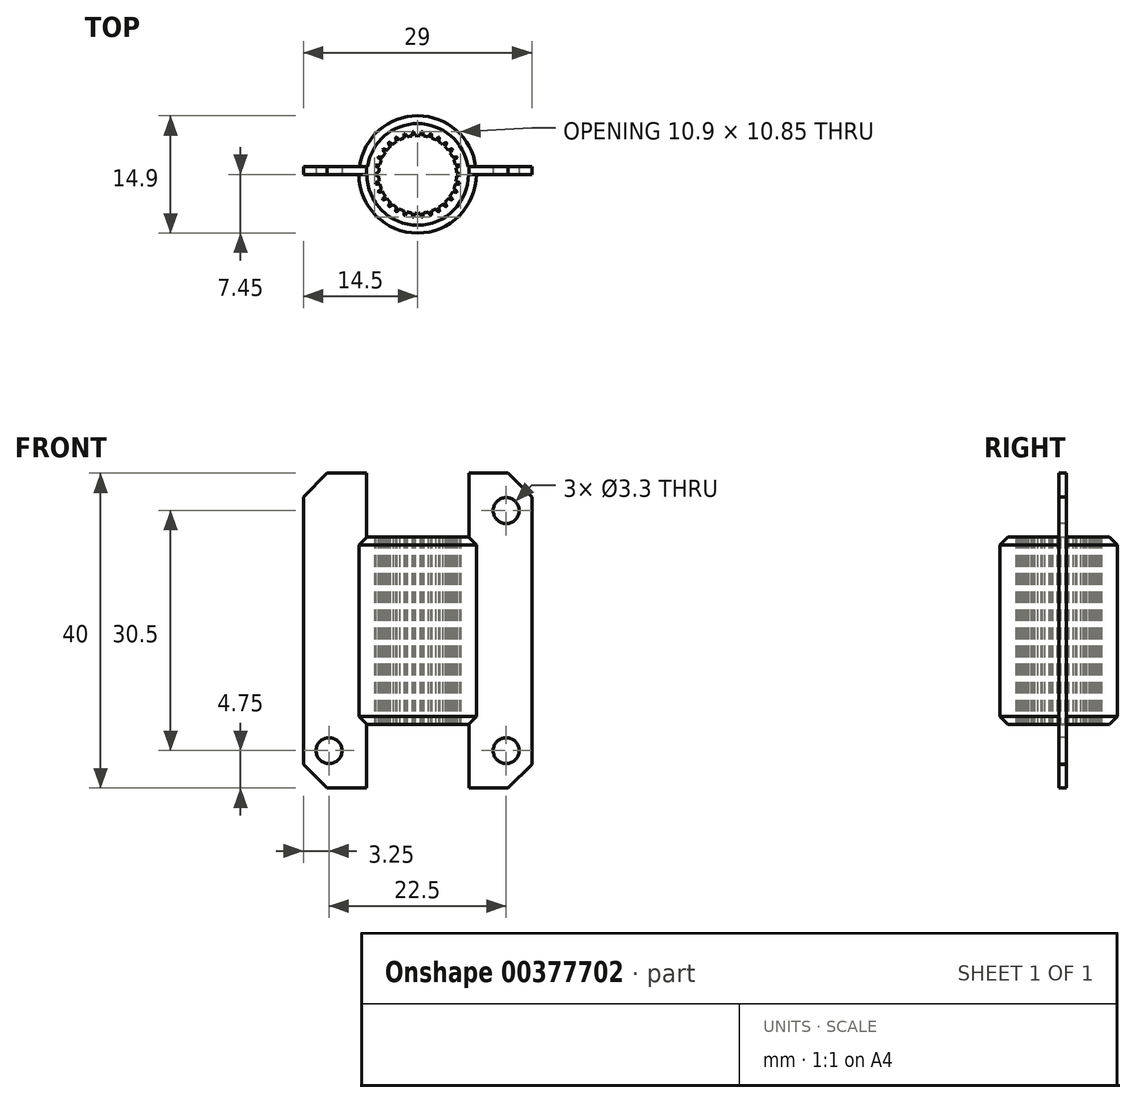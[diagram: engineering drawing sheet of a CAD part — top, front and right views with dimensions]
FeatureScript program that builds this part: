
annotation { "Feature Type Name" : "Feature", "Feature Type Description" : "" }
export const myFeature = defineFeature(function(context is Context, id is Id, definition is map)
    precondition{}
    {
        {
            var Q0;
            Q0=qCreatedBy(makeId("Top.planeOp"),FACE);
            var sketch = newSketch(context, id + "F0", { "sketchPlane" : qUnion([Q0])});
            skCircle(sketch, "E0", {"center": v(0, 0) * mm, "radius": 4.95 * mm, "construction": true});
            skCircle(sketch, "E1", {"center": v(0, 0) * mm, "radius": 7.45 * mm});
            skCircle(sketch, "E2.0", {"center": v(0, 0) * mm, "radius": 5.45 * mm});
            skLineSegment(sketch, "E3", {"start": v(0, 0) * mm, "end": v(0, 9.5) * mm, "construction": true});
            skLineSegment(sketch, "E4", {"start": v(0.5, 5.43) * mm, "end": v(0.3, 4.94) * mm});
            skArc(sketch, "E5", {"start": v(0.3, 4.94) * mm, "mid": v(0.15, 4.95) * mm, "end": v(0, 4.95) * mm});
            skLineSegment(sketch, "E6.MirrorCS", {"start": v(-0.5, 5.43) * mm, "end": v(-0.3, 4.94) * mm});
            skArc(sketch, "E7.MirrorCS", {"start": v(-0.3, 4.94) * mm, "mid": v(-0.15, 4.95) * mm, "end": v(0, 4.95) * mm});
            skLineSegment(sketch, "E8.1.0", {"start": v(-0.64, 5.41) * mm, "end": v(-0.73, 4.9) * mm});
            skLineSegment(sketch, "E8.1.1", {"start": v(-1.62, 5.2) * mm, "end": v(-1.32, 4.77) * mm});
            skArc(sketch, "E8.1.2", {"start": v(-0.73, 4.9) * mm, "mid": v(-0.88, 4.87) * mm, "end": v(-1.03, 4.84) * mm});
            skArc(sketch, "E8.1.3", {"start": v(-1.32, 4.77) * mm, "mid": v(-1.18, 4.8) * mm, "end": v(-1.03, 4.84) * mm});
            skLineSegment(sketch, "E8.2.0", {"start": v(-1.75, 5.16) * mm, "end": v(-1.74, 4.64) * mm});
            skLineSegment(sketch, "E8.2.1", {"start": v(-2.66, 4.75) * mm, "end": v(-2.28, 4.4) * mm});
            skArc(sketch, "E8.2.2", {"start": v(-1.74, 4.64) * mm, "mid": v(-1.88, 4.58) * mm, "end": v(-2.01, 4.52) * mm});
            skArc(sketch, "E8.2.3", {"start": v(-2.28, 4.4) * mm, "mid": v(-2.15, 4.46) * mm, "end": v(-2.01, 4.52) * mm});
            skLineSegment(sketch, "E8.3.0", {"start": v(-2.79, 4.68) * mm, "end": v(-2.66, 4.17) * mm});
            skLineSegment(sketch, "E8.3.1", {"start": v(-3.6, 4.1) * mm, "end": v(-3.15, 3.82) * mm});
            skArc(sketch, "E8.3.2", {"start": v(-2.66, 4.17) * mm, "mid": v(-2.79, 4.1) * mm, "end": v(-2.9, 4) * mm});
            skArc(sketch, "E8.3.3", {"start": v(-3.15, 3.82) * mm, "mid": v(-3.03, 3.91) * mm, "end": v(-2.9, 4) * mm});
            skLineSegment(sketch, "E8.4.0", {"start": v(-3.7, 4) * mm, "end": v(-3.47, 3.53) * mm});
            skLineSegment(sketch, "E8.4.1", {"start": v(-4.37, 3.26) * mm, "end": v(-3.87, 3.08) * mm});
            skArc(sketch, "E8.4.2", {"start": v(-3.47, 3.53) * mm, "mid": v(-3.58, 3.42) * mm, "end": v(-3.68, 3.31) * mm});
            skArc(sketch, "E8.4.3", {"start": v(-3.87, 3.08) * mm, "mid": v(-3.78, 3.2) * mm, "end": v(-3.68, 3.31) * mm});
            skLineSegment(sketch, "E8.5.0", {"start": v(-4.45, 3.15) * mm, "end": v(-4.13, 2.73) * mm});
            skLineSegment(sketch, "E8.5.1", {"start": v(-4.95, 2.28) * mm, "end": v(-4.43, 2.21) * mm});
            skArc(sketch, "E8.5.2", {"start": v(-4.13, 2.73) * mm, "mid": v(-4.2, 2.6) * mm, "end": v(-4.29, 2.48) * mm});
            skArc(sketch, "E8.5.3", {"start": v(-4.43, 2.21) * mm, "mid": v(-4.36, 2.34) * mm, "end": v(-4.29, 2.48) * mm});
            skLineSegment(sketch, "E8.6.0", {"start": v(-5, 2.15) * mm, "end": v(-4.6, 1.81) * mm});
            skLineSegment(sketch, "E8.6.1", {"start": v(-5.32, 1.2) * mm, "end": v(-4.8, 1.24) * mm});
            skArc(sketch, "E8.6.2", {"start": v(-4.6, 1.81) * mm, "mid": v(-4.66, 1.67) * mm, "end": v(-4.7, 1.53) * mm});
            skArc(sketch, "E8.6.3", {"start": v(-4.8, 1.24) * mm, "mid": v(-4.75, 1.39) * mm, "end": v(-4.7, 1.53) * mm});
            skLineSegment(sketch, "E8.7.0", {"start": v(-5.35, 1.06) * mm, "end": v(-4.88, 0.81) * mm});
            skLineSegment(sketch, "E8.7.1", {"start": v(-5.45, 0.07) * mm, "end": v(-4.95, 0.22) * mm});
            skArc(sketch, "E8.7.2", {"start": v(-4.88, 0.81) * mm, "mid": v(-4.9, 0.67) * mm, "end": v(-4.92, 0.52) * mm});
            skArc(sketch, "E8.7.3", {"start": v(-4.95, 0.22) * mm, "mid": v(-4.94, 0.37) * mm, "end": v(-4.92, 0.52) * mm});
            skLineSegment(sketch, "E8.8.0", {"start": v(-5.45, -0.07) * mm, "end": v(-4.95, -0.22) * mm});
            skLineSegment(sketch, "E8.8.1", {"start": v(-5.35, -1.06) * mm, "end": v(-4.88, -0.81) * mm});
            skArc(sketch, "E8.8.2", {"start": v(-4.95, -0.22) * mm, "mid": v(-4.94, -0.37) * mm, "end": v(-4.92, -0.52) * mm});
            skArc(sketch, "E8.8.3", {"start": v(-4.88, -0.81) * mm, "mid": v(-4.9, -0.67) * mm, "end": v(-4.92, -0.52) * mm});
            skLineSegment(sketch, "E8.9.0", {"start": v(-5.32, -1.2) * mm, "end": v(-4.8, -1.24) * mm});
            skLineSegment(sketch, "E8.9.1", {"start": v(-5, -2.15) * mm, "end": v(-4.6, -1.81) * mm});
            skArc(sketch, "E8.9.2", {"start": v(-4.8, -1.24) * mm, "mid": v(-4.75, -1.39) * mm, "end": v(-4.7, -1.53) * mm});
            skArc(sketch, "E8.9.3", {"start": v(-4.6, -1.81) * mm, "mid": v(-4.66, -1.67) * mm, "end": v(-4.7, -1.53) * mm});
            skLineSegment(sketch, "E8.10.0", {"start": v(-4.95, -2.28) * mm, "end": v(-4.43, -2.21) * mm});
            skLineSegment(sketch, "E8.10.1", {"start": v(-4.45, -3.15) * mm, "end": v(-4.13, -2.73) * mm});
            skArc(sketch, "E8.10.2", {"start": v(-4.43, -2.21) * mm, "mid": v(-4.36, -2.34) * mm, "end": v(-4.29, -2.47) * mm});
            skArc(sketch, "E8.10.3", {"start": v(-4.13, -2.73) * mm, "mid": v(-4.2, -2.6) * mm, "end": v(-4.29, -2.47) * mm});
            skLineSegment(sketch, "E8.11.0", {"start": v(-4.37, -3.26) * mm, "end": v(-3.87, -3.08) * mm});
            skLineSegment(sketch, "E8.11.1", {"start": v(-3.7, -4) * mm, "end": v(-3.47, -3.53) * mm});
            skArc(sketch, "E8.11.2", {"start": v(-3.87, -3.08) * mm, "mid": v(-3.78, -3.2) * mm, "end": v(-3.68, -3.31) * mm});
            skArc(sketch, "E8.11.3", {"start": v(-3.47, -3.53) * mm, "mid": v(-3.58, -3.42) * mm, "end": v(-3.68, -3.31) * mm});
            skLineSegment(sketch, "E8.12.0", {"start": v(-3.6, -4.1) * mm, "end": v(-3.15, -3.82) * mm});
            skLineSegment(sketch, "E8.12.1", {"start": v(-2.79, -4.68) * mm, "end": v(-2.66, -4.17) * mm});
            skArc(sketch, "E8.12.2", {"start": v(-3.15, -3.82) * mm, "mid": v(-3.03, -3.91) * mm, "end": v(-2.9, -4) * mm});
            skArc(sketch, "E8.12.3", {"start": v(-2.66, -4.17) * mm, "mid": v(-2.79, -4.1) * mm, "end": v(-2.9, -4) * mm});
            skLineSegment(sketch, "E8.13.0", {"start": v(-2.66, -4.75) * mm, "end": v(-2.28, -4.4) * mm});
            skLineSegment(sketch, "E8.13.1", {"start": v(-1.75, -5.16) * mm, "end": v(-1.74, -4.64) * mm});
            skArc(sketch, "E8.13.2", {"start": v(-2.28, -4.4) * mm, "mid": v(-2.15, -4.46) * mm, "end": v(-2.01, -4.52) * mm});
            skArc(sketch, "E8.13.3", {"start": v(-1.74, -4.64) * mm, "mid": v(-1.88, -4.58) * mm, "end": v(-2.01, -4.52) * mm});
            skLineSegment(sketch, "E8.14.0", {"start": v(-1.62, -5.2) * mm, "end": v(-1.32, -4.77) * mm});
            skLineSegment(sketch, "E8.14.1", {"start": v(-0.64, -5.41) * mm, "end": v(-0.73, -4.9) * mm});
            skArc(sketch, "E8.14.2", {"start": v(-1.32, -4.77) * mm, "mid": v(-1.18, -4.8) * mm, "end": v(-1.03, -4.84) * mm});
            skArc(sketch, "E8.14.3", {"start": v(-0.73, -4.9) * mm, "mid": v(-0.88, -4.87) * mm, "end": v(-1.03, -4.84) * mm});
            skLineSegment(sketch, "E8.15.0", {"start": v(-0.5, -5.43) * mm, "end": v(-0.3, -4.94) * mm});
            skLineSegment(sketch, "E8.15.1", {"start": v(0.5, -5.43) * mm, "end": v(0.3, -4.94) * mm});
            skArc(sketch, "E8.15.2", {"start": v(-0.3, -4.94) * mm, "mid": v(-0.15, -4.95) * mm, "end": v(0, -4.95) * mm});
            skArc(sketch, "E8.15.3", {"start": v(0.3, -4.94) * mm, "mid": v(0.15, -4.95) * mm, "end": v(0, -4.95) * mm});
            skLineSegment(sketch, "E8.16.0", {"start": v(0.64, -5.41) * mm, "end": v(0.73, -4.9) * mm});
            skLineSegment(sketch, "E8.16.1", {"start": v(1.62, -5.2) * mm, "end": v(1.32, -4.77) * mm});
            skArc(sketch, "E8.16.2", {"start": v(0.73, -4.9) * mm, "mid": v(0.88, -4.87) * mm, "end": v(1.03, -4.84) * mm});
            skArc(sketch, "E8.16.3", {"start": v(1.32, -4.77) * mm, "mid": v(1.18, -4.8) * mm, "end": v(1.03, -4.84) * mm});
            skLineSegment(sketch, "E8.17.0", {"start": v(1.75, -5.16) * mm, "end": v(1.74, -4.64) * mm});
            skLineSegment(sketch, "E8.17.1", {"start": v(2.66, -4.75) * mm, "end": v(2.28, -4.4) * mm});
            skArc(sketch, "E8.17.2", {"start": v(1.74, -4.64) * mm, "mid": v(1.88, -4.58) * mm, "end": v(2.01, -4.52) * mm});
            skArc(sketch, "E8.17.3", {"start": v(2.28, -4.4) * mm, "mid": v(2.15, -4.46) * mm, "end": v(2.01, -4.52) * mm});
            skLineSegment(sketch, "E8.18.0", {"start": v(2.79, -4.68) * mm, "end": v(2.66, -4.17) * mm});
            skLineSegment(sketch, "E8.18.1", {"start": v(3.6, -4.1) * mm, "end": v(3.15, -3.82) * mm});
            skArc(sketch, "E8.18.2", {"start": v(2.66, -4.17) * mm, "mid": v(2.79, -4.1) * mm, "end": v(2.9, -4) * mm});
            skArc(sketch, "E8.18.3", {"start": v(3.15, -3.82) * mm, "mid": v(3.03, -3.91) * mm, "end": v(2.9, -4) * mm});
            skLineSegment(sketch, "E8.19.0", {"start": v(3.7, -4) * mm, "end": v(3.47, -3.53) * mm});
            skLineSegment(sketch, "E8.19.1", {"start": v(4.37, -3.26) * mm, "end": v(3.87, -3.08) * mm});
            skArc(sketch, "E8.19.2", {"start": v(3.47, -3.53) * mm, "mid": v(3.58, -3.42) * mm, "end": v(3.68, -3.31) * mm});
            skArc(sketch, "E8.19.3", {"start": v(3.87, -3.08) * mm, "mid": v(3.78, -3.2) * mm, "end": v(3.68, -3.31) * mm});
            skLineSegment(sketch, "E8.20.0", {"start": v(4.45, -3.15) * mm, "end": v(4.13, -2.73) * mm});
            skLineSegment(sketch, "E8.20.1", {"start": v(4.95, -2.28) * mm, "end": v(4.43, -2.21) * mm});
            skArc(sketch, "E8.20.2", {"start": v(4.13, -2.73) * mm, "mid": v(4.2, -2.6) * mm, "end": v(4.29, -2.48) * mm});
            skArc(sketch, "E8.20.3", {"start": v(4.43, -2.21) * mm, "mid": v(4.36, -2.34) * mm, "end": v(4.29, -2.48) * mm});
            skLineSegment(sketch, "E8.21.0", {"start": v(5, -2.15) * mm, "end": v(4.6, -1.81) * mm});
            skLineSegment(sketch, "E8.21.1", {"start": v(5.32, -1.2) * mm, "end": v(4.8, -1.24) * mm});
            skArc(sketch, "E8.21.2", {"start": v(4.6, -1.81) * mm, "mid": v(4.66, -1.67) * mm, "end": v(4.7, -1.53) * mm});
            skArc(sketch, "E8.21.3", {"start": v(4.8, -1.24) * mm, "mid": v(4.75, -1.39) * mm, "end": v(4.7, -1.53) * mm});
            skLineSegment(sketch, "E8.22.0", {"start": v(5.35, -1.06) * mm, "end": v(4.88, -0.81) * mm});
            skLineSegment(sketch, "E8.22.1", {"start": v(5.45, -0.07) * mm, "end": v(4.95, -0.22) * mm});
            skArc(sketch, "E8.22.2", {"start": v(4.88, -0.81) * mm, "mid": v(4.9, -0.67) * mm, "end": v(4.92, -0.52) * mm});
            skArc(sketch, "E8.22.3", {"start": v(4.95, -0.22) * mm, "mid": v(4.94, -0.37) * mm, "end": v(4.92, -0.52) * mm});
            skLineSegment(sketch, "E8.23.0", {"start": v(5.45, 0.07) * mm, "end": v(4.95, 0.22) * mm});
            skLineSegment(sketch, "E8.23.1", {"start": v(5.35, 1.06) * mm, "end": v(4.88, 0.81) * mm});
            skArc(sketch, "E8.23.2", {"start": v(4.95, 0.22) * mm, "mid": v(4.94, 0.37) * mm, "end": v(4.92, 0.52) * mm});
            skArc(sketch, "E8.23.3", {"start": v(4.88, 0.81) * mm, "mid": v(4.9, 0.67) * mm, "end": v(4.92, 0.52) * mm});
            skLineSegment(sketch, "E8.24.0", {"start": v(5.32, 1.2) * mm, "end": v(4.8, 1.24) * mm});
            skLineSegment(sketch, "E8.24.1", {"start": v(5, 2.15) * mm, "end": v(4.6, 1.81) * mm});
            skArc(sketch, "E8.24.2", {"start": v(4.8, 1.24) * mm, "mid": v(4.75, 1.39) * mm, "end": v(4.7, 1.53) * mm});
            skArc(sketch, "E8.24.3", {"start": v(4.6, 1.81) * mm, "mid": v(4.66, 1.67) * mm, "end": v(4.7, 1.53) * mm});
            skLineSegment(sketch, "E8.25.0", {"start": v(4.95, 2.28) * mm, "end": v(4.43, 2.21) * mm});
            skLineSegment(sketch, "E8.25.1", {"start": v(4.45, 3.15) * mm, "end": v(4.13, 2.73) * mm});
            skArc(sketch, "E8.25.2", {"start": v(4.43, 2.21) * mm, "mid": v(4.36, 2.34) * mm, "end": v(4.29, 2.47) * mm});
            skArc(sketch, "E8.25.3", {"start": v(4.13, 2.73) * mm, "mid": v(4.2, 2.6) * mm, "end": v(4.29, 2.47) * mm});
            skLineSegment(sketch, "E8.26.0", {"start": v(4.37, 3.26) * mm, "end": v(3.87, 3.08) * mm});
            skLineSegment(sketch, "E8.26.1", {"start": v(3.7, 4) * mm, "end": v(3.47, 3.53) * mm});
            skArc(sketch, "E8.26.2", {"start": v(3.87, 3.08) * mm, "mid": v(3.78, 3.2) * mm, "end": v(3.68, 3.31) * mm});
            skArc(sketch, "E8.26.3", {"start": v(3.47, 3.53) * mm, "mid": v(3.58, 3.42) * mm, "end": v(3.68, 3.31) * mm});
            skLineSegment(sketch, "E8.27.0", {"start": v(3.6, 4.1) * mm, "end": v(3.15, 3.82) * mm});
            skLineSegment(sketch, "E8.27.1", {"start": v(2.79, 4.68) * mm, "end": v(2.66, 4.17) * mm});
            skArc(sketch, "E8.27.2", {"start": v(3.15, 3.82) * mm, "mid": v(3.03, 3.91) * mm, "end": v(2.9, 4) * mm});
            skArc(sketch, "E8.27.3", {"start": v(2.66, 4.17) * mm, "mid": v(2.79, 4.1) * mm, "end": v(2.9, 4) * mm});
            skLineSegment(sketch, "E8.28.0", {"start": v(2.66, 4.75) * mm, "end": v(2.28, 4.4) * mm});
            skLineSegment(sketch, "E8.28.1", {"start": v(1.75, 5.16) * mm, "end": v(1.74, 4.64) * mm});
            skArc(sketch, "E8.28.2", {"start": v(2.28, 4.4) * mm, "mid": v(2.15, 4.46) * mm, "end": v(2.01, 4.52) * mm});
            skArc(sketch, "E8.28.3", {"start": v(1.74, 4.64) * mm, "mid": v(1.88, 4.58) * mm, "end": v(2.01, 4.52) * mm});
            skLineSegment(sketch, "E8.29.0", {"start": v(1.62, 5.2) * mm, "end": v(1.32, 4.77) * mm});
            skLineSegment(sketch, "E8.29.1", {"start": v(0.64, 5.41) * mm, "end": v(0.73, 4.9) * mm});
            skArc(sketch, "E8.29.2", {"start": v(1.32, 4.77) * mm, "mid": v(1.18, 4.8) * mm, "end": v(1.03, 4.84) * mm});
            skArc(sketch, "E8.29.3", {"start": v(0.73, 4.9) * mm, "mid": v(0.88, 4.87) * mm, "end": v(1.03, 4.84) * mm});
            skSolve(sketch);
        }
        {
            var Q0;
            {var subQ0=sQuery(id+"F0.wireOp",EDGE,"E8.4.0");Q0=makeQuery(id+"F0.imprint","IMPRINT",FACE,{"disambiguationData":[TD([[makeQuery(id+"F0.imprint","IMPRINT",EDGE,{"derivedFrom":subQ0}),-1.0]])]});}
            var Q1;
            {var subQ1=sQuery(id+"F0.wireOp",EDGE,"E8.5.0");Q1=makeQuery(id+"F0.imprint","IMPRINT",FACE,{"disambiguationData":[TD([[makeQuery(id+"F0.imprint","IMPRINT",EDGE,{"derivedFrom":subQ1}),-1.0]])]});}
            var Q2;
            {var subQ1=sQuery(id+"F0.wireOp",EDGE,"E8.3.0");Q2=makeQuery(id+"F0.imprint","IMPRINT",FACE,{"disambiguationData":[TD([[makeQuery(id+"F0.imprint","IMPRINT",EDGE,{"derivedFrom":subQ1}),-1.0]])]});}
            var Q3;
            {var subQ1=sQuery(id+"F0.wireOp",EDGE,"E8.2.0");Q3=makeQuery(id+"F0.imprint","IMPRINT",FACE,{"disambiguationData":[TD([[makeQuery(id+"F0.imprint","IMPRINT",EDGE,{"derivedFrom":subQ1}),-1.0]])]});}
            var Q4;
            {var subQ1=sQuery(id+"F0.wireOp",EDGE,"E8.1.0");Q4=makeQuery(id+"F0.imprint","IMPRINT",FACE,{"disambiguationData":[TD([[makeQuery(id+"F0.imprint","IMPRINT",EDGE,{"derivedFrom":subQ1}),-1.0]])]});}
            var Q5;
            {var subQ1=sQuery(id+"F0.wireOp",EDGE,"E4");Q5=makeQuery(id+"F0.imprint","IMPRINT",FACE,{"disambiguationData":[TD([[makeQuery(id+"F0.imprint","IMPRINT",EDGE,{"derivedFrom":subQ1}),-1.0]])]});}
            var Q6;
            {var subQ0=sQuery(id+"F0.wireOp",EDGE,"E8.29.0");Q6=makeQuery(id+"F0.imprint","IMPRINT",FACE,{"disambiguationData":[TD([[makeQuery(id+"F0.imprint","IMPRINT",EDGE,{"derivedFrom":subQ0}),-1.0]])]});}
            var Q7;
            Q7=makeQuery(id+"F0.imprint","IMPRINT",FACE,{"disambiguationData":[TD([[makeQuery(id+"F0.imprint","IMPRINT",EDGE,{"derivedFrom":sQuery(id+"F0.wireOp",EDGE,"E1")}),1.0]])]});
            var Q8;
            {var subQ1=sQuery(id+"F0.wireOp",EDGE,"E8.28.0");Q8=makeQuery(id+"F0.imprint","IMPRINT",FACE,{"disambiguationData":[TD([[makeQuery(id+"F0.imprint","IMPRINT",EDGE,{"derivedFrom":subQ1}),-1.0]])]});}
            var Q9;
            {var subQ1=sQuery(id+"F0.wireOp",EDGE,"E8.27.0");Q9=makeQuery(id+"F0.imprint","IMPRINT",FACE,{"disambiguationData":[TD([[makeQuery(id+"F0.imprint","IMPRINT",EDGE,{"derivedFrom":subQ1}),-1.0]])]});}
            var Q10;
            {var subQ1=sQuery(id+"F0.wireOp",EDGE,"E8.26.0");Q10=makeQuery(id+"F0.imprint","IMPRINT",FACE,{"disambiguationData":[TD([[makeQuery(id+"F0.imprint","IMPRINT",EDGE,{"derivedFrom":subQ1}),-1.0]])]});}
            var Q11;
            {var subQ1=sQuery(id+"F0.wireOp",EDGE,"E8.25.0");Q11=makeQuery(id+"F0.imprint","IMPRINT",FACE,{"disambiguationData":[TD([[makeQuery(id+"F0.imprint","IMPRINT",EDGE,{"derivedFrom":subQ1}),-1.0]])]});}
            var Q12;
            {var subQ0=sQuery(id+"F0.wireOp",EDGE,"E8.24.0");Q12=makeQuery(id+"F0.imprint","IMPRINT",FACE,{"disambiguationData":[TD([[makeQuery(id+"F0.imprint","IMPRINT",EDGE,{"derivedFrom":subQ0}),-1.0]])]});}
            var Q13;
            {var subQ0=sQuery(id+"F0.wireOp",EDGE,"E8.23.0");Q13=makeQuery(id+"F0.imprint","IMPRINT",FACE,{"disambiguationData":[TD([[makeQuery(id+"F0.imprint","IMPRINT",EDGE,{"derivedFrom":subQ0}),-1.0]])]});}
            var Q14;
            {var subQ1=sQuery(id+"F0.wireOp",EDGE,"E8.6.0");Q14=makeQuery(id+"F0.imprint","IMPRINT",FACE,{"disambiguationData":[TD([[makeQuery(id+"F0.imprint","IMPRINT",EDGE,{"derivedFrom":subQ1}),-1.0]])]});}
            var Q15;
            {var subQ1=sQuery(id+"F0.wireOp",EDGE,"E8.7.0");Q15=makeQuery(id+"F0.imprint","IMPRINT",FACE,{"disambiguationData":[TD([[makeQuery(id+"F0.imprint","IMPRINT",EDGE,{"derivedFrom":subQ1}),-1.0]])]});}
            var Q16;
            {var subQ1=sQuery(id+"F0.wireOp",EDGE,"E8.8.0");Q16=makeQuery(id+"F0.imprint","IMPRINT",FACE,{"disambiguationData":[TD([[makeQuery(id+"F0.imprint","IMPRINT",EDGE,{"derivedFrom":subQ1}),-1.0]])]});}
            var Q17;
            {var subQ0=sQuery(id+"F0.wireOp",EDGE,"E8.9.0");Q17=makeQuery(id+"F0.imprint","IMPRINT",FACE,{"disambiguationData":[TD([[makeQuery(id+"F0.imprint","IMPRINT",EDGE,{"derivedFrom":subQ0}),-1.0]])]});}
            var Q18;
            {var subQ1=sQuery(id+"F0.wireOp",EDGE,"E8.10.0");Q18=makeQuery(id+"F0.imprint","IMPRINT",FACE,{"disambiguationData":[TD([[makeQuery(id+"F0.imprint","IMPRINT",EDGE,{"derivedFrom":subQ1}),-1.0]])]});}
            var Q19;
            {var subQ1=sQuery(id+"F0.wireOp",EDGE,"E8.11.0");Q19=makeQuery(id+"F0.imprint","IMPRINT",FACE,{"disambiguationData":[TD([[makeQuery(id+"F0.imprint","IMPRINT",EDGE,{"derivedFrom":subQ1}),-1.0]])]});}
            var Q20;
            {var subQ1=sQuery(id+"F0.wireOp",EDGE,"E8.12.0");Q20=makeQuery(id+"F0.imprint","IMPRINT",FACE,{"disambiguationData":[TD([[makeQuery(id+"F0.imprint","IMPRINT",EDGE,{"derivedFrom":subQ1}),-1.0]])]});}
            var Q21;
            {var subQ1=sQuery(id+"F0.wireOp",EDGE,"E8.13.0");Q21=makeQuery(id+"F0.imprint","IMPRINT",FACE,{"disambiguationData":[TD([[makeQuery(id+"F0.imprint","IMPRINT",EDGE,{"derivedFrom":subQ1}),-1.0]])]});}
            var Q22;
            {var subQ0=sQuery(id+"F0.wireOp",EDGE,"E8.14.0");Q22=makeQuery(id+"F0.imprint","IMPRINT",FACE,{"disambiguationData":[TD([[makeQuery(id+"F0.imprint","IMPRINT",EDGE,{"derivedFrom":subQ0}),-1.0]])]});}
            var Q23;
            {var subQ1=sQuery(id+"F0.wireOp",EDGE,"E8.15.0");Q23=makeQuery(id+"F0.imprint","IMPRINT",FACE,{"disambiguationData":[TD([[makeQuery(id+"F0.imprint","IMPRINT",EDGE,{"derivedFrom":subQ1}),-1.0]])]});}
            var Q24;
            {var subQ1=sQuery(id+"F0.wireOp",EDGE,"E8.16.0");Q24=makeQuery(id+"F0.imprint","IMPRINT",FACE,{"disambiguationData":[TD([[makeQuery(id+"F0.imprint","IMPRINT",EDGE,{"derivedFrom":subQ1}),-1.0]])]});}
            var Q25;
            {var subQ1=sQuery(id+"F0.wireOp",EDGE,"E8.17.0");Q25=makeQuery(id+"F0.imprint","IMPRINT",FACE,{"disambiguationData":[TD([[makeQuery(id+"F0.imprint","IMPRINT",EDGE,{"derivedFrom":subQ1}),-1.0]])]});}
            var Q26;
            {var subQ1=sQuery(id+"F0.wireOp",EDGE,"E8.18.0");Q26=makeQuery(id+"F0.imprint","IMPRINT",FACE,{"disambiguationData":[TD([[makeQuery(id+"F0.imprint","IMPRINT",EDGE,{"derivedFrom":subQ1}),-1.0]])]});}
            var Q27;
            {var subQ0=sQuery(id+"F0.wireOp",EDGE,"E8.19.0");Q27=makeQuery(id+"F0.imprint","IMPRINT",FACE,{"disambiguationData":[TD([[makeQuery(id+"F0.imprint","IMPRINT",EDGE,{"derivedFrom":subQ0}),-1.0]])]});}
            var Q28;
            {var subQ0=sQuery(id+"F0.wireOp",EDGE,"E8.20.0");Q28=makeQuery(id+"F0.imprint","IMPRINT",FACE,{"disambiguationData":[TD([[makeQuery(id+"F0.imprint","IMPRINT",EDGE,{"derivedFrom":subQ0}),-1.0]])]});}
            var Q29;
            {var subQ1=sQuery(id+"F0.wireOp",EDGE,"E8.21.0");Q29=makeQuery(id+"F0.imprint","IMPRINT",FACE,{"disambiguationData":[TD([[makeQuery(id+"F0.imprint","IMPRINT",EDGE,{"derivedFrom":subQ1}),-1.0]])]});}
            var Q30;
            {var subQ1=sQuery(id+"F0.wireOp",EDGE,"E8.22.0");Q30=makeQuery(id+"F0.imprint","IMPRINT",FACE,{"disambiguationData":[TD([[makeQuery(id+"F0.imprint","IMPRINT",EDGE,{"derivedFrom":subQ1}),-1.0]])]});}
            extrude(context, id + "F1", {"entities" : qUnion([Q0, Q1, Q2, Q3, Q4, Q5, Q6, Q7, Q8, Q9, Q10, Q11, Q12, Q13, Q14, Q15, Q16, Q17, Q18, Q19, Q20, Q21, Q22, Q23, Q24, Q25, Q26, Q27, Q28, Q29, Q30]), "endBound" : BoundingType.SYMMETRIC, "depth" : 23.8 * mm});
        }
        {
            var Q0;
            Q0=qCreatedBy(makeId("Front.planeOp"),FACE);
            var sketch = newSketch(context, id + "F2", { "sketchPlane" : qUnion([Q0])});
            skLineSegment(sketch, "E9.bottom", {"start": v(-14.5, -20) * mm, "end": v(14.5, -20) * mm});
            skLineSegment(sketch, "E9.top", {"start": v(-14.5, 20) * mm, "end": v(14.5, 20) * mm});
            skLineSegment(sketch, "E9.left", {"start": v(-14.5, -20) * mm, "end": v(-14.5, 0) * mm});
            skLineSegment(sketch, "E9.right", {"start": v(14.5, -20) * mm, "end": v(14.5, 0) * mm});
            skPoint(sketch, "E9.middle", {"position": v(0, 0) * mm});
            skCircle(sketch, "E10", {"center": v(-11.25, -15.25) * mm, "radius": 1.65 * mm});
            skCircle(sketch, "E11.MirrorC", {"center": v(-11.25, 15.25) * mm, "radius": 1.65 * mm});
            skCircle(sketch, "E12.MirrorC", {"center": v(11.25, -15.25) * mm, "radius": 1.65 * mm});
            skCircle(sketch, "E13.MirrorC", {"center": v(11.25, 15.25) * mm, "radius": 1.65 * mm});
            skLineSegment(sketch, "E14", {"start": v(7.45, 12) * mm, "end": v(7.45, -12) * mm});
            skLineSegment(sketch, "E15.left", {"start": v(-6.5, -20) * mm, "end": v(-6.5, 20) * mm});
            skLineSegment(sketch, "E15.right", {"start": v(6.5, -20) * mm, "end": v(6.5, 20) * mm});
            skLineSegment(sketch, "E16.trimOffspring", {"start": v(-14.5, 0) * mm, "end": v(-14.5, 20) * mm});
            skLineSegment(sketch, "E17.trimOffspring", {"start": v(14.5, 0) * mm, "end": v(14.5, 20) * mm});
            skSolve(sketch);
        }
        {
            var Q0;
            {var subQ0=sQuery(id+"F2.wireOp",EDGE,"E9.left");Q0=makeQuery(id+"F2.imprint","IMPRINT",FACE,{"disambiguationData":[TD([[makeQuery(id+"F2.imprint","IMPRINT",EDGE,{"derivedFrom":subQ0}),-1.0]])]});}
            var Q1;
            {var subQ0=sQuery(id+"F2.wireOp",EDGE,"E9.right");Q1=makeQuery(id+"F2.imprint","IMPRINT",FACE,{"disambiguationData":[TD([[makeQuery(id+"F2.imprint","IMPRINT",EDGE,{"derivedFrom":subQ0}),1.0]])]});}
            var Q2;
            Q2=makeQuery(id+"F2.imprint","IMPRINT",FACE,{"disambiguationData":[TD([[makeQuery(id+"F2.imprint","IMPRINT",EDGE,{"derivedFrom":sQuery(id+"F2.wireOp",EDGE,"E11.MirrorC")}),1.0]])]});
            var Q3;
            Q3=makeQuery(id+"F2.imprint","IMPRINT",FACE,{"disambiguationData":[TD([[makeQuery(id+"F2.imprint","IMPRINT",EDGE,{"derivedFrom":sQuery(id+"F2.wireOp",EDGE,"E13.MirrorC")}),-1.0]])]});
            extrude(context, id + "F3", {"entities" : qUnion([Q0, Q1, Q2, Q3]), "operationType" : NewBodyOperationType.ADD, "oppositeDirection" : true, "depth" : 1 * mm});
        }
        {
            var Q0;
            Q0=makeQuery(id+"F1.opExtrude","CAP_EDGE",EDGE,{"disambiguationData":[OSD([sQuery(id+"F0.wireOp",EDGE,"E1")])],"isStart":true});
            var Q1;
            Q1=makeQuery(id+"F1.opExtrude","CAP_EDGE",EDGE,{"disambiguationData":[OSD([sQuery(id+"F0.wireOp",EDGE,"E1")])],"isStart":false});
            chamfer(context, id + "F4", {"entities" : qUnion([Q0, Q1]), "width" : 1 * mm, "tangentPropagation" : true});
        }
        {
            var Q0;
            Q0=makeQuery(id+"F3.opExtrude","SWEPT_EDGE",EDGE,{"disambiguationData":[OSD([sQuery(id+"F2.wireOp",EDGE,"E9.top"),sQuery(id+"F2.wireOp",EDGE,"E16.trimOffspring")])]});
            var Q1;
            Q1=makeQuery(id+"F3.opExtrude","SWEPT_EDGE",EDGE,{"disambiguationData":[OSD([sQuery(id+"F2.wireOp",EDGE,"E9.top"),sQuery(id+"F2.wireOp",EDGE,"E17.trimOffspring")])]});
            var Q2;
            Q2=makeQuery(id+"F3.opExtrude","SWEPT_EDGE",EDGE,{"disambiguationData":[OSD([sQuery(id+"F2.wireOp",EDGE,"E9.bottom"),sQuery(id+"F2.wireOp",EDGE,"E9.right")])]});
            var Q3;
            Q3=makeQuery(id+"F3.opExtrude","SWEPT_EDGE",EDGE,{"disambiguationData":[OSD([sQuery(id+"F2.wireOp",EDGE,"E9.bottom"),sQuery(id+"F2.wireOp",EDGE,"E9.left")])]});
            chamfer(context, id + "F5", {"entities" : qUnion([Q0, Q1, Q2, Q3]), "width" : 3 * mm, "tangentPropagation" : true});
        }
    });
